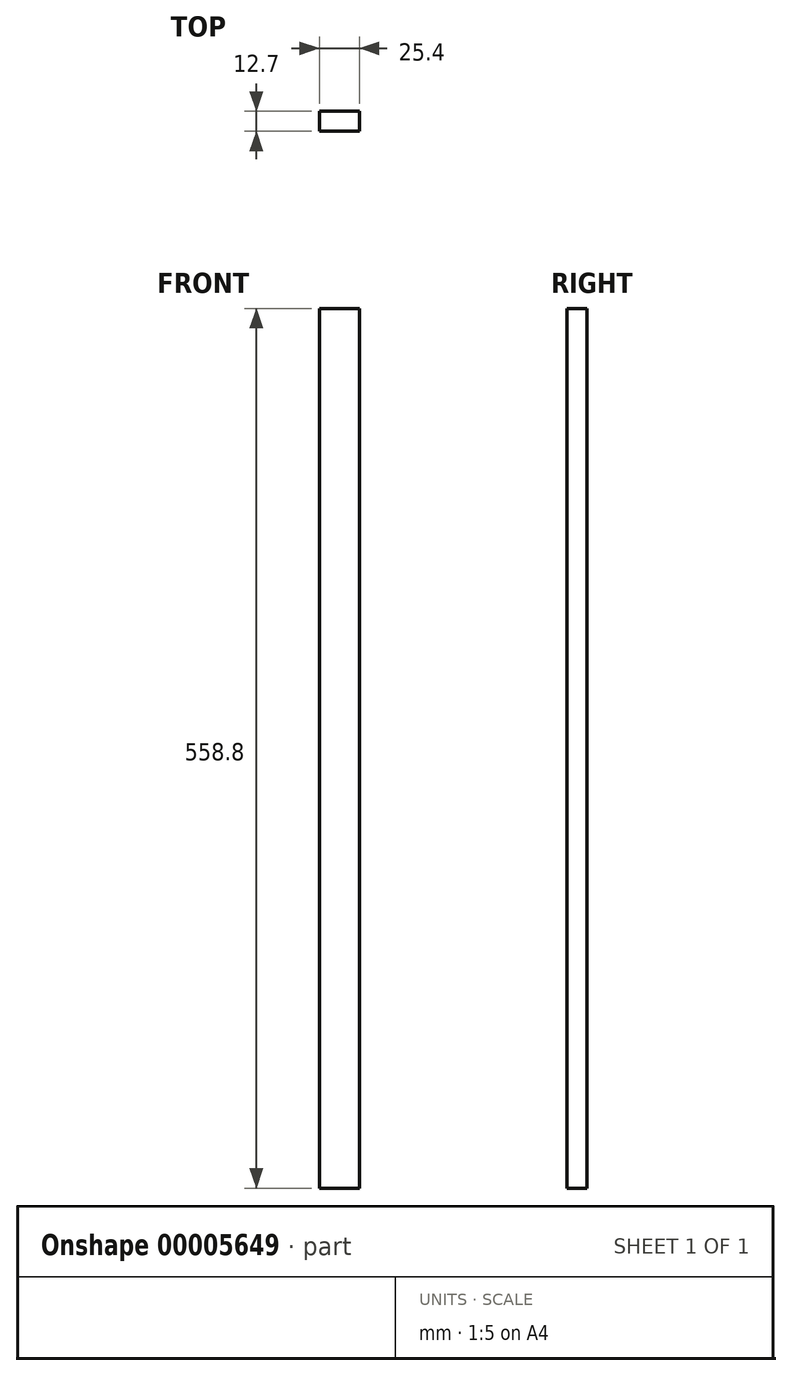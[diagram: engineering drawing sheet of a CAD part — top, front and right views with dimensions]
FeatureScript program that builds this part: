
annotation { "Feature Type Name" : "Feature", "Feature Type Description" : "" }
export const myFeature = defineFeature(function(context is Context, id is Id, definition is map)
    precondition{}
    {
        {
            var Q0;
            Q0=qCreatedBy(makeId("Front.planeOp"),FACE);
            var sketch = newSketch(context, id + "F0", { "sketchPlane" : qUnion([Q0])});
            skLineSegment(sketch, "E0.bottom", {"start": v(0, 0) * mm, "end": v(25.4, 0) * mm});
            skLineSegment(sketch, "E0.top", {"start": v(0, 558.8) * mm, "end": v(25.4, 558.8) * mm});
            skLineSegment(sketch, "E0.left", {"start": v(0, 0) * mm, "end": v(0, 558.8) * mm});
            skLineSegment(sketch, "E0.right", {"start": v(25.4, 0) * mm, "end": v(25.4, 558.8) * mm});
            skSolve(sketch);
        }
        {
            var Q0;
            Q0 = qSketchRegion(id + "F0", true);
            extrude(context, id + "F1", {"entities" : qUnion([Q0]), "depth" : 12.7 * mm});
        }
    });
